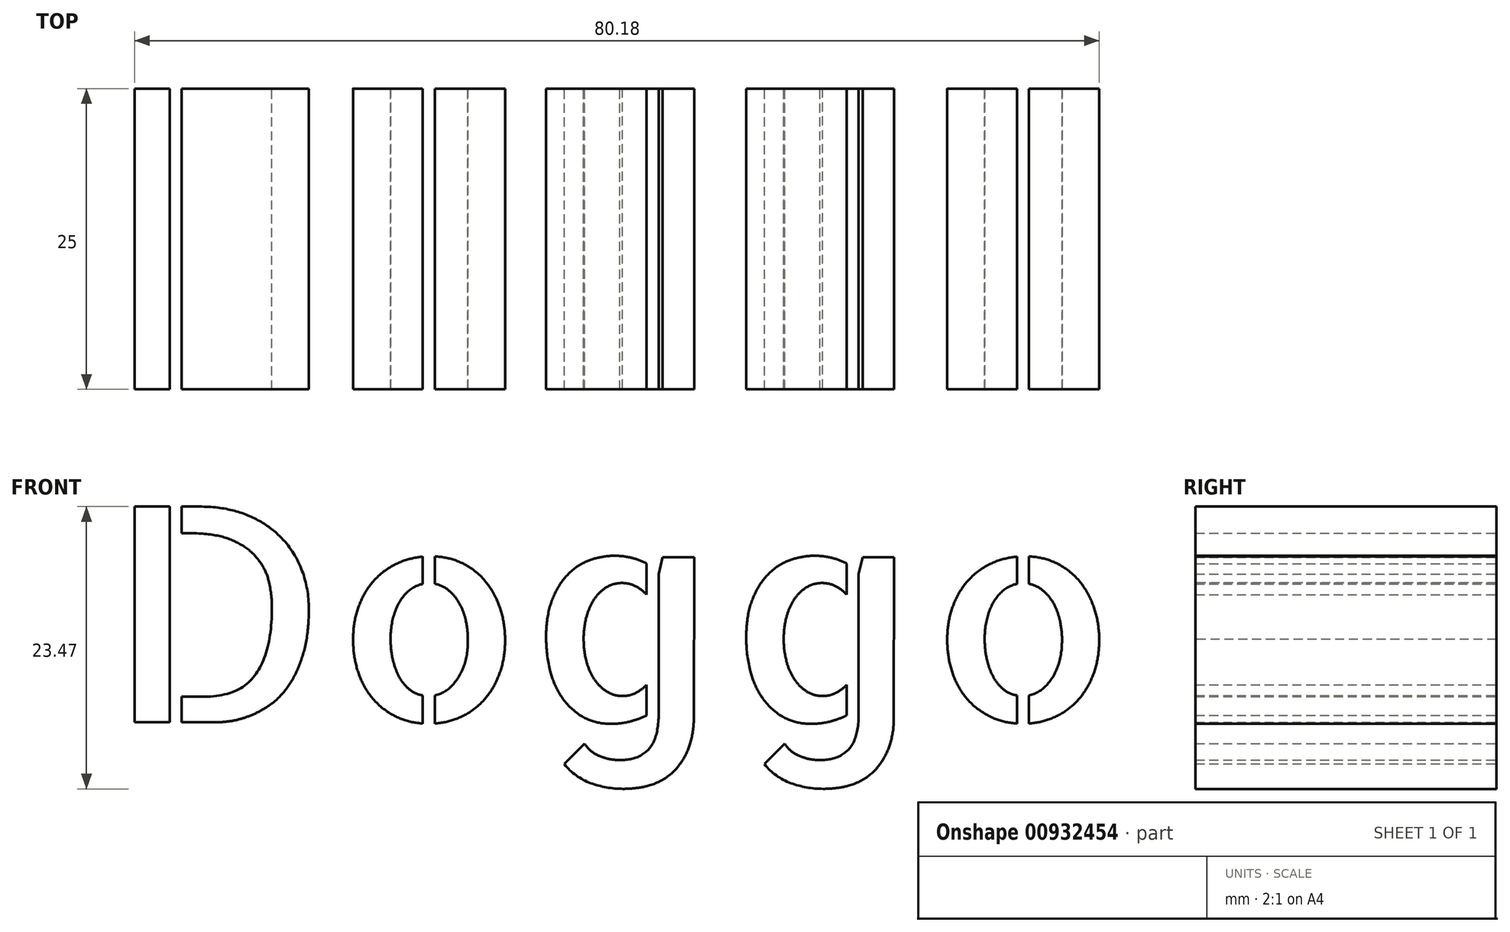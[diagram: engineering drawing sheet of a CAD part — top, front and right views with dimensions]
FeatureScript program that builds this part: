
annotation { "Feature Type Name" : "Feature", "Feature Type Description" : "" }
export const myFeature = defineFeature(function(context is Context, id is Id, definition is map)
    precondition{}
    {
        {
            var Q0;
            Q0=qCreatedBy(makeId("Front.planeOp"),FACE);
            var sketch = newSketch(context, id + "F0", { "sketchPlane" : qUnion([Q0])});
            skText(sketch, "E0", { "text": "Doggo", "fontName": "AllertaStencil-Regular.ttf"});
            const initialGuessF0  = {"E0": [-0.037, -0.01795, 1, 0, 0.01795]};
            skSetInitialGuess(sketch, initialGuessF0);
            skSolve(sketch);
        }
        {
            var Q0;
            Q0 = qSketchRegion(id + "F0", true);
            extrude(context, id + "F1", {"entities" : qUnion([Q0]), "depth" : 25 * mm, "offsetDistance" : 25 * mm});
        }
    });
